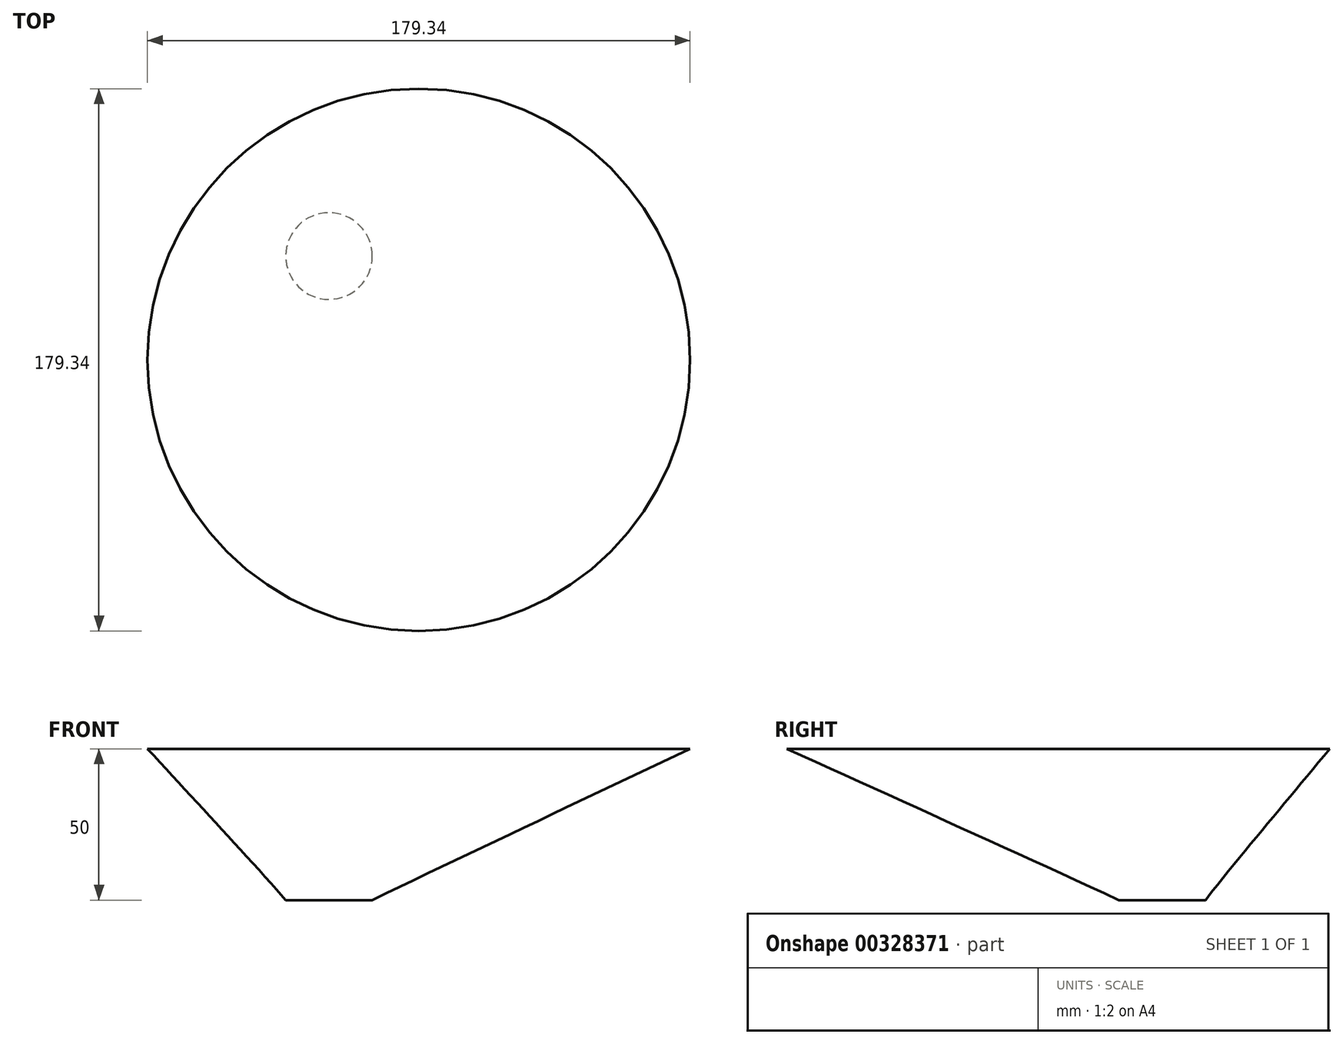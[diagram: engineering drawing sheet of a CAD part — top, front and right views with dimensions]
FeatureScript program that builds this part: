
annotation { "Feature Type Name" : "Feature", "Feature Type Description" : "" }
export const myFeature = defineFeature(function(context is Context, id is Id, definition is map)
    precondition{}
    {
        {
            var Q0;
            Q0=qCreatedBy(makeId("Top.planeOp"),FACE);
            cPlane(context, id + "F0", {"entities" : qUnion([Q0]), "cplaneType" : CPlaneType.OFFSET, "offset" : 50 * mm, "width" : 150 * mm, "height" : 150 * mm});
        }
        {
            var Q0;
            Q0=qCreatedBy(id+"F0.planeOp",FACE);
            var sketch = newSketch(context, id + "F1", { "sketchPlane" : qUnion([Q0])});
            skCircle(sketch, "E0", {"center": v(0, 0) * mm, "radius": 89.67 * mm});
            skSolve(sketch);
        }
        {
            var Q0;
            Q0=qCreatedBy(makeId("Top.planeOp"),FACE);
            var sketch = newSketch(context, id + "F2", { "sketchPlane" : qUnion([Q0])});
            skCircle(sketch, "E1", {"center": v(-29.68, 34.33) * mm, "radius": 14.32 * mm});
            skSolve(sketch);
        }
        {
            var Q0;
            Q0 = qSketchRegion(id + "F1", true);
            var Q1;
            Q1 = qSketchRegion(id + "F2", true);
            loft(context, id + "F3", {"sheetProfilesArray" : [{ "sheetProfileEntities" : qUnion([Q0]) }, { "sheetProfileEntities" : qUnion([Q1]) }]});
        }
    });
